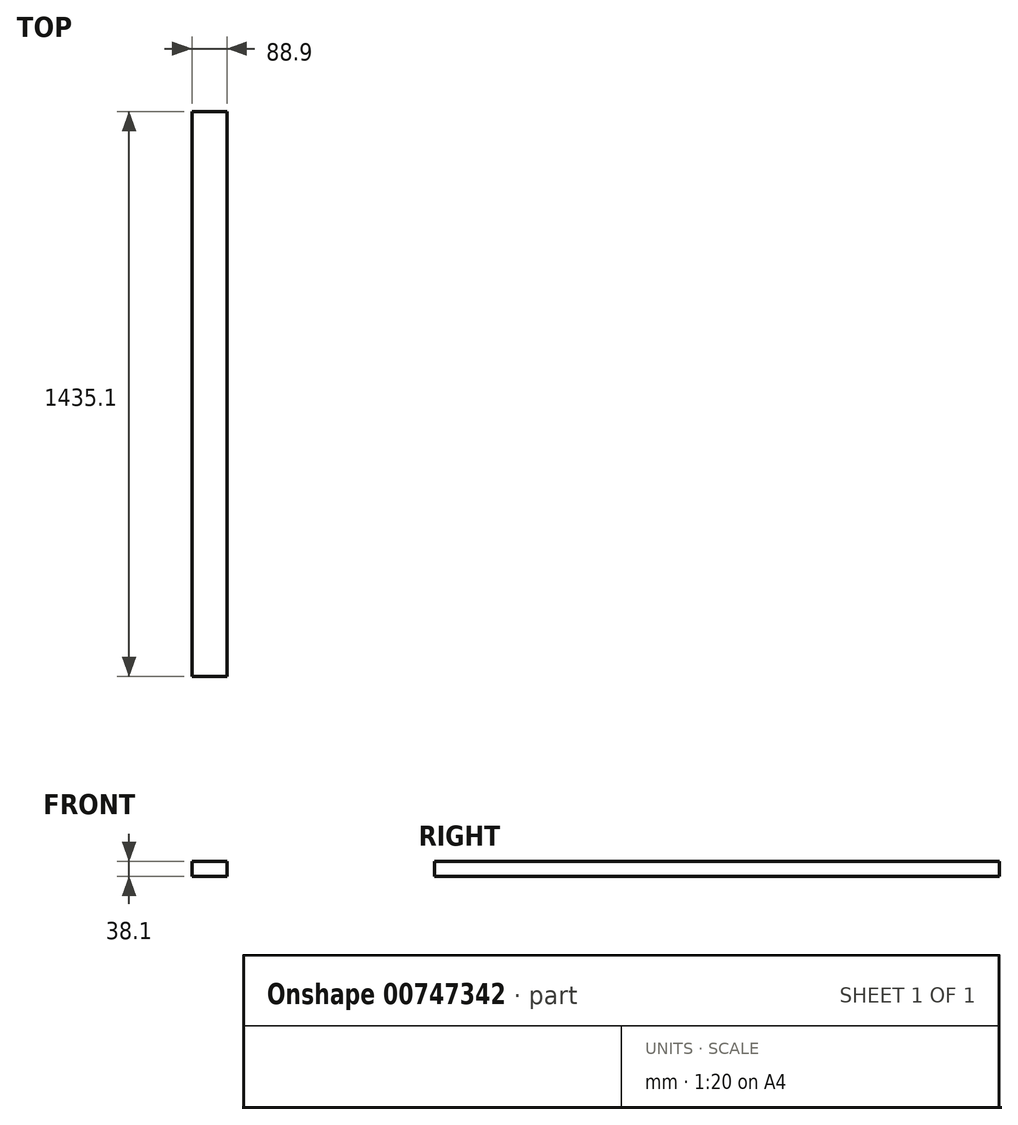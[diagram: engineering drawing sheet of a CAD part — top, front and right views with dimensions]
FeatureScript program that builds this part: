
annotation { "Feature Type Name" : "Feature", "Feature Type Description" : "" }
export const myFeature = defineFeature(function(context is Context, id is Id, definition is map)
    precondition{}
    {
        {
            var Q0;
            Q0=qCreatedBy(makeId("Front.planeOp"),FACE);
            var sketch = newSketch(context, id + "F0", { "sketchPlane" : qUnion([Q0])});
            skLineSegment(sketch, "E0.bottom", {"start": v(0, 0) * mm, "end": v(88.9, 0) * mm});
            skLineSegment(sketch, "E0.top", {"start": v(0, 38.1) * mm, "end": v(88.9, 38.1) * mm});
            skLineSegment(sketch, "E0.left", {"start": v(0, 0) * mm, "end": v(0, 38.1) * mm});
            skLineSegment(sketch, "E0.right", {"start": v(88.9, 0) * mm, "end": v(88.9, 38.1) * mm});
            skSolve(sketch);
        }
        {
            var Q0;
            Q0 = qSketchRegion(id + "F0", true);
            extrude(context, id + "F1", {"entities" : qUnion([Q0]), "depth" : 1435.1 * mm, "offsetDistance" : 25.4 * mm});
        }
    });
